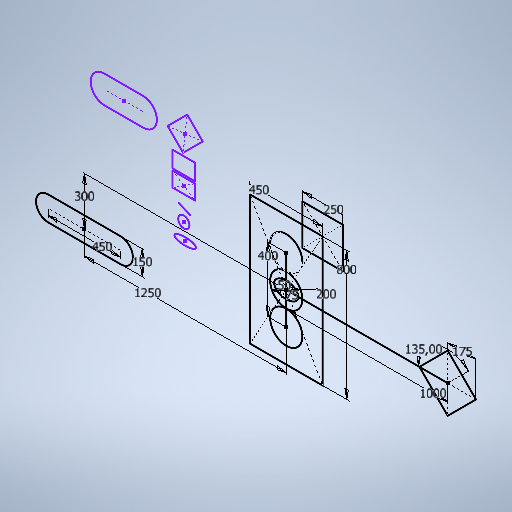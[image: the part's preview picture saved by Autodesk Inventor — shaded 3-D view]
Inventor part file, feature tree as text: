
AUTODESK INVENTOR PART (.ipt)
format: ipt  version: 2025.2 (Build 292293000, 293)  size: 292,864 bytes
history: native  units: mm
features: sketch x1
ambient origin geometry x8: Origin, YZ Plane, XZ Plane, XY Plane, X Axis, Y Axis, Z Axis, Center Point
feature tree (1):
  sketch  "Esboço1"  dims[d0=400.0mm d1=200.0mm d2=75.0mm d3=50.0mm d4=450.0mm d5=800.0mm d6=250.0mm d7=1000.0mm d8=175.0mm d9=135.0deg d10=450.0mm d11=300.0mm d12=1250.0mm d13=150.0mm]
